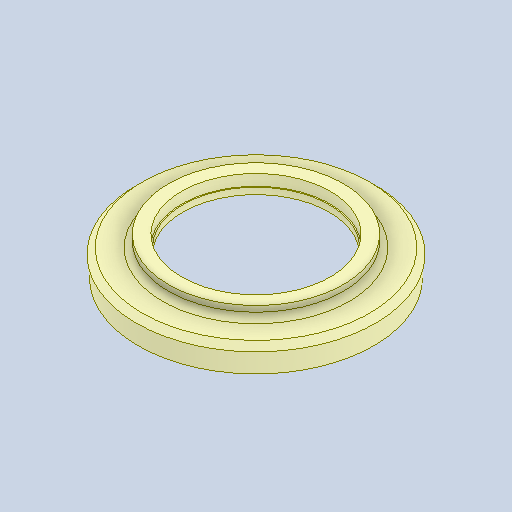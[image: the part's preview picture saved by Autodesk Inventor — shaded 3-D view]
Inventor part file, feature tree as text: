
AUTODESK INVENTOR PART (.ipt)
format: ipt  version: 2024.1 (Build 281209000, 209)  size: 140,288 bytes
history: native  units: in
note: dims shown in document units (in); Inventor stores cm internally (conversion verified against a paired STEP export)
features: fillet x1
ambient origin geometry x8: Origin, YZ Plane, XZ Plane, XY Plane, X Axis, Y Axis, Z Axis, Center Point
bodies: Solid1 (feature_tree)
feature tree (1):
  fillet  "Fillet1"  [1 undecoded]
note: 1 required parameter value undecoded (feature->parameter linkage not recoverable at this tier; creation-order binding heuristic only, values carry confidence <= 0.55)
